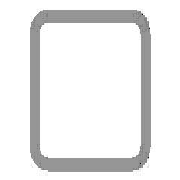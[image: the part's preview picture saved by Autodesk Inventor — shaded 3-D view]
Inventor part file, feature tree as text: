
AUTODESK INVENTOR PART (.ipt)
format: ipt  version: 2022 (Build 260153000, 153)  size: 156,160 bytes
history: native  units: mm (DEFAULTED — no unit token found)
features: other x4, plane x3, sketch x3, split x2, extrude x1
ambient origin geometry x8: Origin, YZ Plane, XZ Plane, XY Plane, X Axis, Y Axis, Z Axis, Center Point
bodies: Solid1 (feature_tree)
feature tree (13):
  parser-record x1  (decoder bookkeeping rows leaked as tree rows — omitted from the tree; the rows remain in map.json)
  other  "Driven Length"
  other  "Plano inicial"
  other  "Plano final"
  extrude  "Cuerpo"  TaperAngle=0.0deg  [1 undecoded]
  plane  "Plano de trabajo4"
  split  "Dividir1"
  plane  "Plano de trabajo5"
  split  "Dividir2"
  sketch  "Boceto"  dims[d10=40.0mm d11=40.0mm d12=5.0mm d13=-11.768067mm d14=211.095123mm d15=20.0mm d16=20.0mm d17=90.0deg d18=222.86319mm]
  sketch  "Sketch3"  dims[d3=222.86319mm d4=0.0mm]
  plane  "Work Plane3"
  sketch  "Sketch4"  dims[d7=7.5mm]
note: 1 required parameter value undecoded (feature->parameter linkage not recoverable at this tier; creation-order binding heuristic only, values carry confidence <= 0.55)
